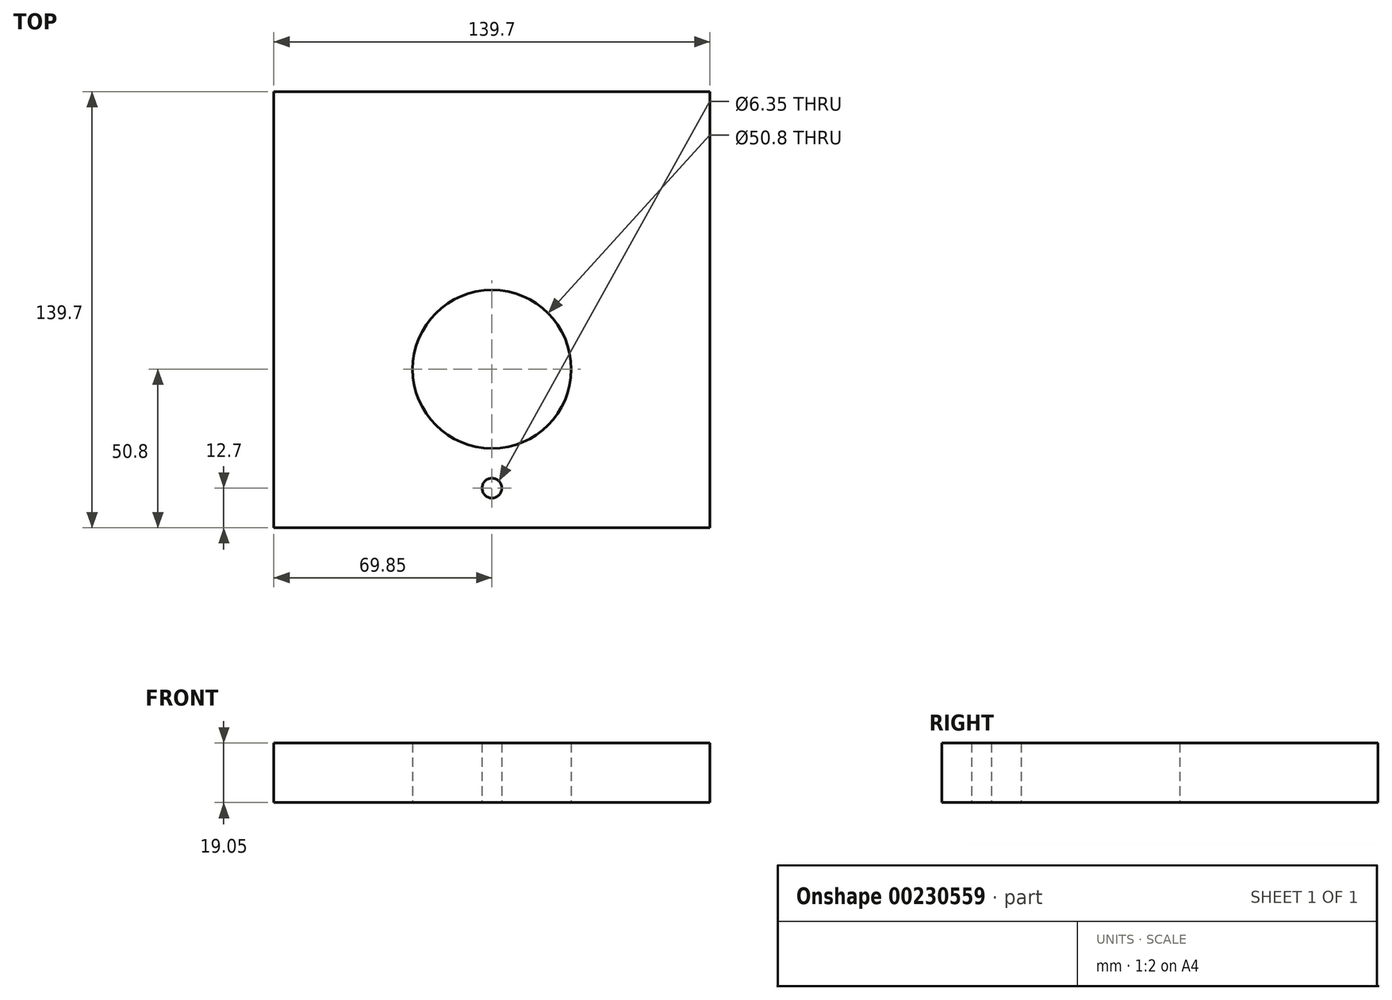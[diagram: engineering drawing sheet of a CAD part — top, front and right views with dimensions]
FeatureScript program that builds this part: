
annotation { "Feature Type Name" : "Feature", "Feature Type Description" : "" }
export const myFeature = defineFeature(function(context is Context, id is Id, definition is map)
    precondition{}
    {
        {
            var Q0;
            Q0=qCreatedBy(makeId("Top.planeOp"),FACE);
            var sketch = newSketch(context, id + "F0", { "sketchPlane" : qUnion([Q0])});
            skLineSegment(sketch, "E0.bottom", {"start": v(-69.85, 73.24) * mm, "end": v(69.85, 73.24) * mm});
            skLineSegment(sketch, "E0.top", {"start": v(-69.85, -66.46) * mm, "end": v(69.85, -66.46) * mm});
            skLineSegment(sketch, "E0.left", {"start": v(-69.85, 73.24) * mm, "end": v(-69.85, -66.46) * mm});
            skLineSegment(sketch, "E0.right", {"start": v(69.85, 73.24) * mm, "end": v(69.85, -66.46) * mm});
            skPoint(sketch, "E0.middle", {"position": v(0, 3.39) * mm});
            skLineSegment(sketch, "E1", {"start": v(0, -66.46) * mm, "end": v(0, -53.76) * mm});
            skPoint(sketch, "E1.endSnap0", {"position": v(0, -66.46) * mm});
            skCircle(sketch, "E2", {"center": v(0, -53.76) * mm, "radius": 3.18 * mm});
            skLineSegment(sketch, "E3", {"start": v(0, -53.76) * mm, "end": v(0, -15.66) * mm});
            skCircle(sketch, "E4", {"center": v(0, -15.66) * mm, "radius": 25.4 * mm});
            skSolve(sketch);
        }
        {
            var Q0;
            Q0 = qSketchRegion(id + "F0", true);
            extrude(context, id + "F1", {"entities" : qUnion([Q0]), "depth" : 19.05 * mm});
        }
    });
